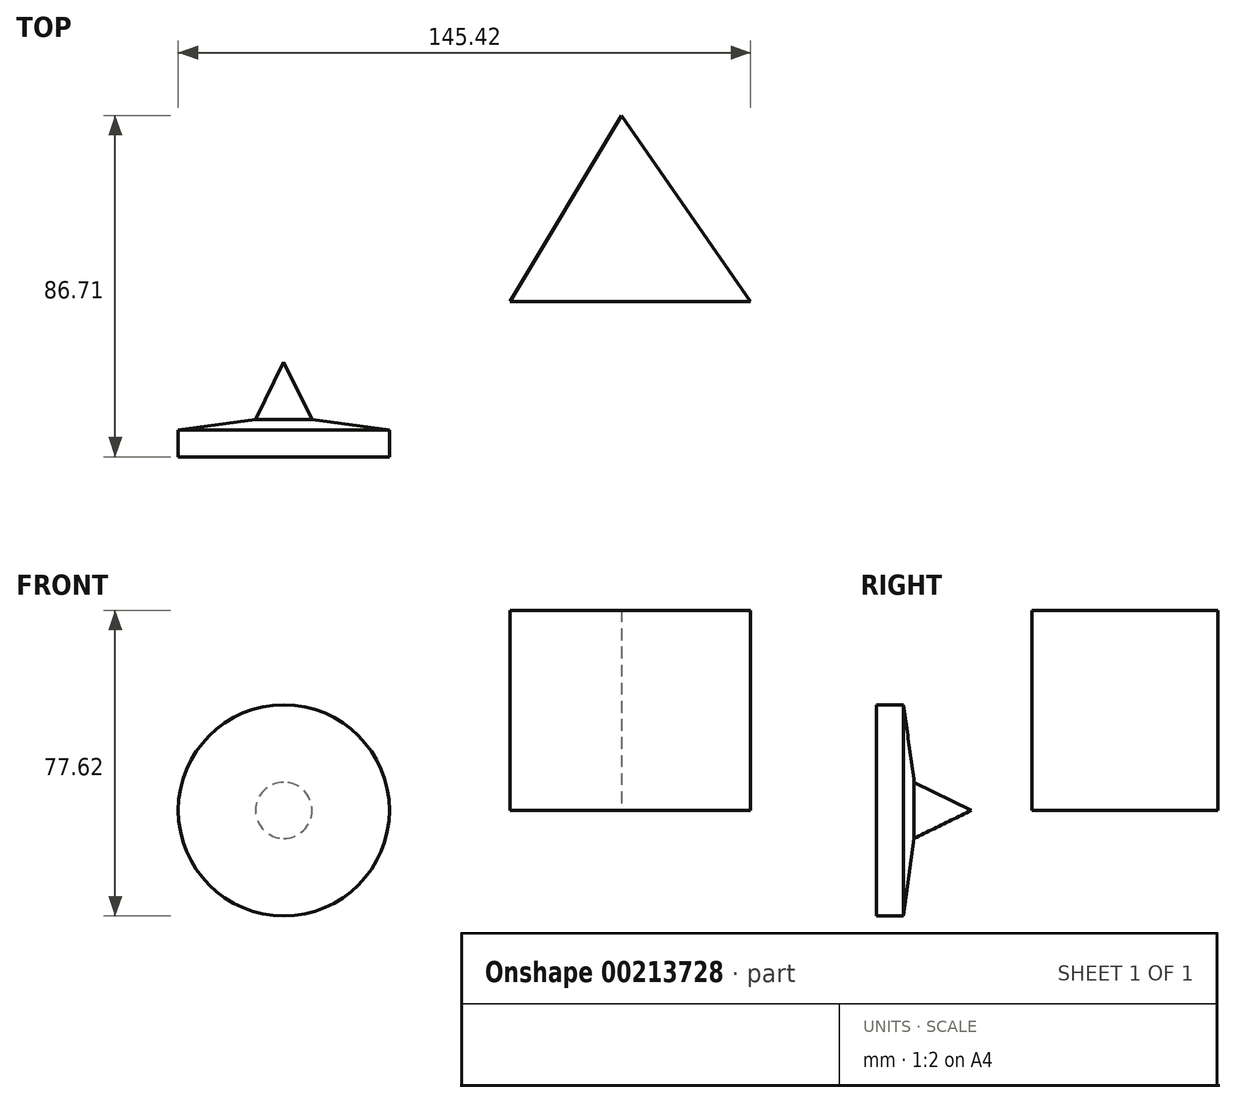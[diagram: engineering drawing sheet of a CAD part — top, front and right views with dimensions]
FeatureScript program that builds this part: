
annotation { "Feature Type Name" : "Feature", "Feature Type Description" : "" }
export const myFeature = defineFeature(function(context is Context, id is Id, definition is map)
    precondition{}
    {
        {
            var Q0;
            Q0=qCreatedBy(makeId("Top.planeOp"),FACE);
            var sketch = newSketch(context, id + "F0", { "sketchPlane" : qUnion([Q0])});
            skLineSegment(sketch, "E0", {"start": v(0, 0) * mm, "end": v(28.3, 47.23) * mm});
            skLineSegment(sketch, "E1", {"start": v(28.3, 47.23) * mm, "end": v(61.09, 0) * mm});
            skLineSegment(sketch, "E2", {"start": v(61.09, 0) * mm, "end": v(0, 0) * mm});
            skSolve(sketch);
        }
        {
            var Q0;
            Q0=makeQuery(id+"F0.imprint","IMPRINT",FACE,{"disambiguationData":[TD([[makeQuery(id+"F0.imprint","IMPRINT",EDGE,{"derivedFrom":sQuery(id+"F0.wireOp",EDGE,"E0")}),-1.0]])]});
            extrude(context, id + "F1", {"entities" : qUnion([Q0]), "depth" : 50.8 * mm});
        }
        {
            var Q0;
            Q0=qCreatedBy(makeId("Top.planeOp"),FACE);
            var sketch = newSketch(context, id + "F2", { "sketchPlane" : qUnion([Q0])});
            skLineSegment(sketch, "E3", {"start": v(-57.51, -15.35) * mm, "end": v(-57.51, -39.48) * mm});
            skLineSegment(sketch, "E4", {"start": v(-57.51, -39.48) * mm, "end": v(-30.7, -39.48) * mm});
            skLineSegment(sketch, "E5", {"start": v(-30.7, -39.48) * mm, "end": v(-30.7, -32.63) * mm});
            skLineSegment(sketch, "E6", {"start": v(-30.7, -32.63) * mm, "end": v(-50.36, -29.95) * mm});
            skLineSegment(sketch, "E7", {"start": v(-50.36, -29.95) * mm, "end": v(-57.51, -15.35) * mm});
            skSolve(sketch);
        }
        {
            var Q0;
            Q0=makeQuery(id+"F2.imprint","IMPRINT",FACE,{"disambiguationData":[TD([[makeQuery(id+"F2.imprint","IMPRINT",EDGE,{"derivedFrom":sQuery(id+"F2.wireOp",EDGE,"E3")}),1.0]])]});
            var Q1;
            Q1=sQuery(id+"F2.wireOp",EDGE,"E3");
            revolve(context, id + "F3", {"entities" : qUnion([Q0]), "axis" : qUnion([Q1]), "revolveType" : RevolveType.FULL});
        }
    });
